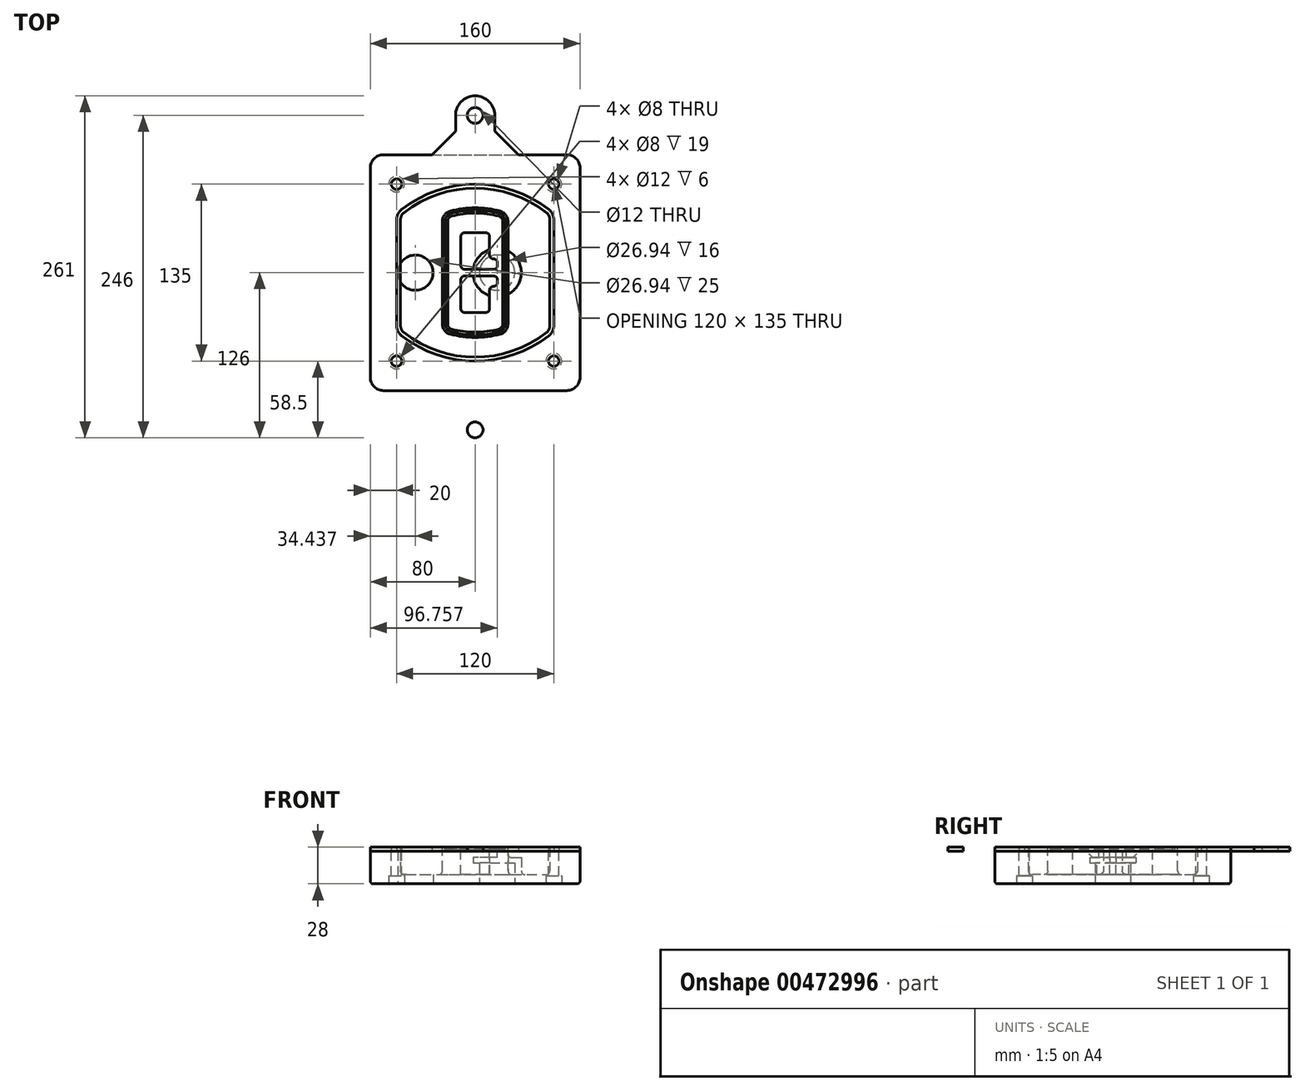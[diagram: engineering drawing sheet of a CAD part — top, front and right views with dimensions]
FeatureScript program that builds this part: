
annotation { "Feature Type Name" : "Feature", "Feature Type Description" : "" }
export const myFeature = defineFeature(function(context is Context, id is Id, definition is map)
    precondition{}
    {
        {
            var Q0;
            Q0=qCreatedBy(makeId("Top.planeOp"),FACE);
            var sketch = newSketch(context, id + "F0", { "sketchPlane" : qUnion([Q0])});
            skPoint(sketch, "E0.rect.middle", {"position": v(0, 0) * mm});
            skLineSegment(sketch, "E1.bottom", {"start": v(-70, -90) * mm, "end": v(70, -90) * mm});
            skLineSegment(sketch, "E1.top", {"start": v(-70, 90) * mm, "end": v(70, 90) * mm});
            skLineSegment(sketch, "E1.left", {"start": v(-80, -80) * mm, "end": v(-80, 80) * mm});
            skLineSegment(sketch, "E1.right", {"start": v(80, -80) * mm, "end": v(80, 80) * mm});
            skLineSegment(sketch, "E2", {"start": v(-80, 90) * mm, "end": v(80, -90) * mm, "construction": true});
            skLineSegment(sketch, "E3", {"start": v(80, 90) * mm, "end": v(-80, -90) * mm, "construction": true});
            skCircle(sketch, "E4", {"center": v(-60, 67.5) * mm, "radius": 4 * mm});
            skCircle(sketch, "E5", {"center": v(60, 67.5) * mm, "radius": 4 * mm});
            skCircle(sketch, "E6", {"center": v(60, -67.5) * mm, "radius": 4 * mm});
            skCircle(sketch, "E7", {"center": v(-60, -67.5) * mm, "radius": 4 * mm});
            skLineSegment(sketch, "E8", {"start": v(-60, 67.5) * mm, "end": v(60, 67.5) * mm, "construction": true});
            skLineSegment(sketch, "E9", {"start": v(60, 67.5) * mm, "end": v(60, -67.5) * mm, "construction": true});
            skLineSegment(sketch, "E10", {"start": v(60, -67.5) * mm, "end": v(-60, -67.5) * mm, "construction": true});
            skLineSegment(sketch, "E11", {"start": v(-60, -67.5) * mm, "end": v(-60, 67.5) * mm, "construction": true});
            skLineSegment(sketch, "E12", {"start": v(-60, 40.3) * mm, "end": v(-60, -40.3) * mm});
            skLineSegment(sketch, "E13", {"start": v(60, 40.3) * mm, "end": v(60, -40.3) * mm});
            skArc(sketch, "E14", {"start": v(56.15, 48.18) * mm, "mid": v(0, 67.5) * mm, "end": v(-56.15, 48.18) * mm});
            skArc(sketch, "E15", {"start": v(-56.15, -48.18) * mm, "mid": v(0, -67.5) * mm, "end": v(56.15, -48.18) * mm});
            skLineSegment(sketch, "E16", {"start": v(-60, 0) * mm, "end": v(60, 0) * mm, "construction": true});
            skPoint(sketch, "E17.visualSharp", {"position": v(-60, -45) * mm});
            skArc(sketch, "E17.filletArc", {"start": v(-60, -40.3) * mm, "mid": v(-58.99, -44.68) * mm, "end": v(-56.15, -48.18) * mm});
            skPoint(sketch, "E18.visualSharp", {"position": v(-60, 45) * mm});
            skArc(sketch, "E18.filletArc", {"start": v(-56.15, 48.18) * mm, "mid": v(-58.99, 44.68) * mm, "end": v(-60, 40.3) * mm});
            skPoint(sketch, "E19.visualSharp", {"position": v(60, 45) * mm});
            skArc(sketch, "E19.filletArc", {"start": v(60, 40.3) * mm, "mid": v(58.99, 44.68) * mm, "end": v(56.15, 48.18) * mm});
            skPoint(sketch, "E20.visualSharp", {"position": v(60, -45) * mm});
            skArc(sketch, "E20.filletArc", {"start": v(56.15, -48.18) * mm, "mid": v(58.99, -44.68) * mm, "end": v(60, -40.3) * mm});
            skPoint(sketch, "E21.visualSharp", {"position": v(-80, 90) * mm});
            skArc(sketch, "E21.filletArc", {"start": v(-70, 90) * mm, "mid": v(-77.07, 87.07) * mm, "end": v(-80, 80) * mm});
            skPoint(sketch, "E22.visualSharp", {"position": v(80, 90) * mm});
            skArc(sketch, "E22.filletArc", {"start": v(80, 80) * mm, "mid": v(77.07, 87.07) * mm, "end": v(70, 90) * mm});
            skPoint(sketch, "E23.visualSharp", {"position": v(80, -90) * mm});
            skArc(sketch, "E23.filletArc", {"start": v(70, -90) * mm, "mid": v(77.07, -87.07) * mm, "end": v(80, -80) * mm});
            skPoint(sketch, "E24.visualSharp", {"position": v(-80, -90) * mm});
            skArc(sketch, "E24.filletArc", {"start": v(-80, -80) * mm, "mid": v(-77.07, -87.07) * mm, "end": v(-70, -90) * mm});
            skArc(sketch, "E25.0", {"start": v(57, 40.3) * mm, "mid": v(56.3, 43.36) * mm, "end": v(54.3, 45.81) * mm});
            skLineSegment(sketch, "E25.1", {"start": v(57, 40.3) * mm, "end": v(57, -40.3) * mm});
            skArc(sketch, "E25.2", {"start": v(54.3, -45.81) * mm, "mid": v(56.3, -43.36) * mm, "end": v(57, -40.3) * mm});
            skArc(sketch, "E25.3", {"start": v(-54.3, -45.81) * mm, "mid": v(0, -64.5) * mm, "end": v(54.3, -45.81) * mm});
            skArc(sketch, "E25.4", {"start": v(-57, -40.3) * mm, "mid": v(-56.3, -43.36) * mm, "end": v(-54.3, -45.81) * mm});
            skArc(sketch, "E25.5", {"start": v(54.3, 45.81) * mm, "mid": v(0, 64.5) * mm, "end": v(-54.3, 45.81) * mm});
            skLineSegment(sketch, "E25.6", {"start": v(-57, 40.3) * mm, "end": v(-57, -40.3) * mm});
            skArc(sketch, "E25.7", {"start": v(-54.3, 45.81) * mm, "mid": v(-56.3, 43.36) * mm, "end": v(-57, 40.3) * mm});
            skArc(sketch, "E26.0", {"start": v(-58.62, 51.33) * mm, "mid": v(-62.58, 46.43) * mm, "end": v(-64, 40.3) * mm});
            skArc(sketch, "E26.1", {"start": v(58.62, 51.33) * mm, "mid": v(0, 71.5) * mm, "end": v(-58.62, 51.33) * mm});
            skArc(sketch, "E26.2", {"start": v(64, 40.3) * mm, "mid": v(62.58, 46.43) * mm, "end": v(58.62, 51.33) * mm});
            skLineSegment(sketch, "E26.3", {"start": v(64, 40.3) * mm, "end": v(64, -40.3) * mm});
            skArc(sketch, "E26.4", {"start": v(58.62, -51.33) * mm, "mid": v(62.58, -46.43) * mm, "end": v(64, -40.3) * mm});
            skLineSegment(sketch, "E26.5", {"start": v(-64, 40.3) * mm, "end": v(-64, -40.3) * mm});
            skArc(sketch, "E26.6", {"start": v(-58.62, -51.33) * mm, "mid": v(0, -71.5) * mm, "end": v(58.62, -51.33) * mm});
            skArc(sketch, "E26.7", {"start": v(-64, -40.3) * mm, "mid": v(-62.58, -46.43) * mm, "end": v(-58.62, -51.33) * mm});
            skSolve(sketch);
        }
        {
            var Q0;
            Q0=makeQuery(id+"F0.imprint","IMPRINT",FACE,{"disambiguationData":[TD([[makeQuery(id+"F0.imprint","IMPRINT",EDGE,{"derivedFrom":sQuery(id+"F0.wireOp",EDGE,"E1.bottom")}),1.0]])]});
            var Q1;
            Q1=makeQuery(id+"F0.imprint","IMPRINT",FACE,{"disambiguationData":[TD([[makeQuery(id+"F0.imprint","IMPRINT",EDGE,{"derivedFrom":sQuery(id+"F0.wireOp",EDGE,"E12")}),1.0]])]});
            var Q2;
            Q2=makeQuery(id+"F0.imprint","IMPRINT",FACE,{"disambiguationData":[TD([[makeQuery(id+"F0.imprint","IMPRINT",EDGE,{"derivedFrom":sQuery(id+"F0.wireOp",EDGE,"E25.0")}),1.0]])]});
            var Q3;
            Q3=makeQuery(id+"F0.imprint","IMPRINT",FACE,{"disambiguationData":[TD([[makeQuery(id+"F0.imprint","IMPRINT",EDGE,{"derivedFrom":sQuery(id+"F0.wireOp",EDGE,"E12")}),-1.0]])]});
            extrude(context, id + "F1", {"entities" : qUnion([Q0, Q1, Q2, Q3]), "oppositeDirection" : true, "depth" : 25 * mm});
        }
        {
            var Q0;
            Q0=makeQuery(id+"F0.imprint","IMPRINT",FACE,{"disambiguationData":[TD([[makeQuery(id+"F0.imprint","IMPRINT",EDGE,{"derivedFrom":sQuery(id+"F0.wireOp",EDGE,"E12")}),1.0]])]});
            extrude(context, id + "F2", {"entities" : qUnion([Q0]), "operationType" : NewBodyOperationType.ADD, "depth" : 3 * mm});
        }
        {
            var Q0;
            Q0=makeQuery(id+"F0.imprint","IMPRINT",FACE,{"disambiguationData":[TD([[makeQuery(id+"F0.imprint","IMPRINT",EDGE,{"derivedFrom":sQuery(id+"F0.wireOp",EDGE,"E25.0")}),1.0]])]});
            extrude(context, id + "F3", {"entities" : qUnion([Q0]), "operationType" : NewBodyOperationType.REMOVE, "oppositeDirection" : true, "depth" : 18 * mm});
        }
        {
            var Q0;
            Q0=makeQuery(id+"F2.opExtrude","CAP_FACE",FACE,{"disambiguationData":[OSD([sQuery(id+"F0.wireOp",EDGE,"E12"),sQuery(id+"F0.wireOp",EDGE,"E13"),sQuery(id+"F0.wireOp",EDGE,"E14"),sQuery(id+"F0.wireOp",EDGE,"E15"),sQuery(id+"F0.wireOp",EDGE,"E17.filletArc"),sQuery(id+"F0.wireOp",EDGE,"E18.filletArc"),sQuery(id+"F0.wireOp",EDGE,"E19.filletArc"),sQuery(id+"F0.wireOp",EDGE,"E20.filletArc"),sQuery(id+"F0.wireOp",EDGE,"E25.0"),sQuery(id+"F0.wireOp",EDGE,"E25.1"),sQuery(id+"F0.wireOp",EDGE,"E25.2"),sQuery(id+"F0.wireOp",EDGE,"E25.3"),sQuery(id+"F0.wireOp",EDGE,"E25.4"),sQuery(id+"F0.wireOp",EDGE,"E25.5"),sQuery(id+"F0.wireOp",EDGE,"E25.6"),sQuery(id+"F0.wireOp",EDGE,"E25.7")])],"isStart":false});
            var sketch = newSketch(context, id + "F4", { "sketchPlane" : qUnion([Q0])});
            skArc(sketch, "E27.0", {"start": v(-19.08, -46.97) * mm, "mid": v(0, -49.5) * mm, "end": v(19.08, -46.97) * mm});
            skArc(sketch, "E28.0", {"start": v(19.08, 46.97) * mm, "mid": v(0, 49.5) * mm, "end": v(-19.08, 46.97) * mm});
            skLineSegment(sketch, "E29", {"start": v(-25, 39.25) * mm, "end": v(-25, -39.25) * mm});
            skLineSegment(sketch, "E30", {"start": v(25, 39.25) * mm, "end": v(25, -39.25) * mm});
            skLineSegment(sketch, "E31", {"start": v(-25, 45.1) * mm, "end": v(25, 45.1) * mm, "construction": true});
            skLineSegment(sketch, "E32", {"start": v(-25, -45.1) * mm, "end": v(25, -45.1) * mm, "construction": true});
            skPoint(sketch, "E33.visualSharp", {"position": v(-25, 45.1) * mm});
            skArc(sketch, "E33.filletArc", {"start": v(-19.08, 46.97) * mm, "mid": v(-23.35, 44.11) * mm, "end": v(-25, 39.25) * mm});
            skPoint(sketch, "E34.visualSharp", {"position": v(25, 45.1) * mm});
            skArc(sketch, "E34.filletArc", {"start": v(25, 39.25) * mm, "mid": v(23.35, 44.11) * mm, "end": v(19.08, 46.97) * mm});
            skPoint(sketch, "E35.visualSharp", {"position": v(25, -45.1) * mm});
            skArc(sketch, "E35.filletArc", {"start": v(19.08, -46.97) * mm, "mid": v(23.35, -44.11) * mm, "end": v(25, -39.25) * mm});
            skPoint(sketch, "E36.visualSharp", {"position": v(-25, -45.1) * mm});
            skArc(sketch, "E36.filletArc", {"start": v(-25, -39.25) * mm, "mid": v(-23.35, -44.11) * mm, "end": v(-19.08, -46.97) * mm});
            skArc(sketch, "E37.0", {"start": v(54.3, 45.81) * mm, "mid": v(0, 64.5) * mm, "end": v(-54.3, 45.81) * mm});
            skArc(sketch, "E37.1", {"start": v(-54.3, 45.81) * mm, "mid": v(-56.3, 43.36) * mm, "end": v(-57, 40.3) * mm});
            skLineSegment(sketch, "E37.2", {"start": v(-57, 40.3) * mm, "end": v(-57, -40.3) * mm});
            skArc(sketch, "E37.3", {"start": v(-57, -40.3) * mm, "mid": v(-56.3, -43.36) * mm, "end": v(-54.3, -45.81) * mm});
            skArc(sketch, "E37.4", {"start": v(-54.3, -45.81) * mm, "mid": v(0, -64.5) * mm, "end": v(54.3, -45.81) * mm});
            skArc(sketch, "E37.5", {"start": v(54.3, -45.81) * mm, "mid": v(56.3, -43.36) * mm, "end": v(57, -40.3) * mm});
            skLineSegment(sketch, "E37.6", {"start": v(57, 40.3) * mm, "end": v(57, -40.3) * mm});
            skArc(sketch, "E37.7", {"start": v(57, 40.3) * mm, "mid": v(56.3, 43.36) * mm, "end": v(54.3, 45.81) * mm});
            skLineSegment(sketch, "E38.0", {"start": v(23, 39.25) * mm, "end": v(23, -39.25) * mm});
            skArc(sketch, "E38.1", {"start": v(18.56, -45.04) * mm, "mid": v(21.76, -42.9) * mm, "end": v(23, -39.25) * mm});
            skArc(sketch, "E38.2", {"start": v(-18.56, -45.04) * mm, "mid": v(0, -47.5) * mm, "end": v(18.56, -45.04) * mm});
            skArc(sketch, "E38.3", {"start": v(-23, -39.25) * mm, "mid": v(-21.76, -42.9) * mm, "end": v(-18.56, -45.04) * mm});
            skLineSegment(sketch, "E38.4", {"start": v(-23, 39.25) * mm, "end": v(-23, -39.25) * mm});
            skArc(sketch, "E38.5", {"start": v(23, 39.25) * mm, "mid": v(21.76, 42.9) * mm, "end": v(18.56, 45.04) * mm});
            skArc(sketch, "E38.6", {"start": v(-18.56, 45.04) * mm, "mid": v(-21.76, 42.9) * mm, "end": v(-23, 39.25) * mm});
            skArc(sketch, "E38.7", {"start": v(18.56, 45.04) * mm, "mid": v(0, 47.5) * mm, "end": v(-18.56, 45.04) * mm});
            skArc(sketch, "E39.0", {"start": v(21, 39.25) * mm, "mid": v(20.18, 41.68) * mm, "end": v(18.04, 43.1) * mm});
            skLineSegment(sketch, "E39.1", {"start": v(21, 39.25) * mm, "end": v(21, -39.25) * mm});
            skArc(sketch, "E39.2", {"start": v(18.04, -43.1) * mm, "mid": v(20.18, -41.68) * mm, "end": v(21, -39.25) * mm});
            skArc(sketch, "E39.3", {"start": v(-18.04, -43.1) * mm, "mid": v(0, -45.5) * mm, "end": v(18.04, -43.1) * mm});
            skArc(sketch, "E39.4", {"start": v(-21, -39.25) * mm, "mid": v(-20.18, -41.68) * mm, "end": v(-18.04, -43.1) * mm});
            skArc(sketch, "E39.5", {"start": v(18.04, 43.1) * mm, "mid": v(0, 45.5) * mm, "end": v(-18.04, 43.1) * mm});
            skLineSegment(sketch, "E39.6", {"start": v(-21, 39.25) * mm, "end": v(-21, -39.25) * mm});
            skArc(sketch, "E39.7", {"start": v(-18.04, 43.1) * mm, "mid": v(-20.18, 41.68) * mm, "end": v(-21, 39.25) * mm});
            skLineSegment(sketch, "E40", {"start": v(-25, 0) * mm, "end": v(25, 0) * mm, "construction": true});
            skLineSegment(sketch, "E41", {"start": v(-11, 5.5) * mm, "end": v(-11, 27.5) * mm});
            skLineSegment(sketch, "E42", {"start": v(-8, 30.5) * mm, "end": v(8, 30.5) * mm});
            skLineSegment(sketch, "E43", {"start": v(11, 27.5) * mm, "end": v(11, 13.5) * mm});
            skLineSegment(sketch, "E44", {"start": v(14, 10.5) * mm, "end": v(14, 10.5) * mm});
            skLineSegment(sketch, "E45", {"start": v(17, 7.5) * mm, "end": v(17, 5.5) * mm});
            skLineSegment(sketch, "E46", {"start": v(14, 2.5) * mm, "end": v(-8, 2.5) * mm});
            skPoint(sketch, "E47.visualSharp", {"position": v(-11, 30.5) * mm});
            skArc(sketch, "E47.filletArc", {"start": v(-8, 30.5) * mm, "mid": v(-10.12, 29.62) * mm, "end": v(-11, 27.5) * mm});
            skPoint(sketch, "E48.visualSharp", {"position": v(11, 30.5) * mm});
            skArc(sketch, "E48.filletArc", {"start": v(11, 27.5) * mm, "mid": v(10.12, 29.62) * mm, "end": v(8, 30.5) * mm});
            skPoint(sketch, "E49.visualSharp", {"position": v(11, 10.5) * mm});
            skArc(sketch, "E49.filletArc", {"start": v(11, 13.5) * mm, "mid": v(11.88, 11.38) * mm, "end": v(14, 10.5) * mm});
            skPoint(sketch, "E50.visualSharp", {"position": v(17, 10.5) * mm});
            skArc(sketch, "E50.filletArc", {"start": v(17, 7.5) * mm, "mid": v(16.12, 9.62) * mm, "end": v(14, 10.5) * mm});
            skPoint(sketch, "E51.visualSharp", {"position": v(17, 2.5) * mm});
            skArc(sketch, "E51.filletArc", {"start": v(14, 2.5) * mm, "mid": v(16.12, 3.38) * mm, "end": v(17, 5.5) * mm});
            skPoint(sketch, "E52.visualSharp", {"position": v(-11, 2.5) * mm});
            skArc(sketch, "E52.filletArc", {"start": v(-11, 5.5) * mm, "mid": v(-10.12, 3.38) * mm, "end": v(-8, 2.5) * mm});
            skLineSegment(sketch, "E53.0.MirrorCS", {"start": v(14, -2.5) * mm, "end": v(-8, -2.5) * mm});
            skArc(sketch, "E54.0.MirrorCS", {"start": v(-11, -5.5) * mm, "mid": v(-10.12, -3.38) * mm, "end": v(-8, -2.5) * mm});
            skLineSegment(sketch, "E55.0.MirrorCS", {"start": v(-11, -5.5) * mm, "end": v(-11, -27.5) * mm});
            skArc(sketch, "E56.0.MirrorCS", {"start": v(-8, -30.5) * mm, "mid": v(-10.12, -29.62) * mm, "end": v(-11, -27.5) * mm});
            skLineSegment(sketch, "E57.0.MirrorCS", {"start": v(-8, -30.5) * mm, "end": v(8, -30.5) * mm});
            skArc(sketch, "E58.0.MirrorCS", {"start": v(11, -27.5) * mm, "mid": v(10.12, -29.62) * mm, "end": v(8, -30.5) * mm});
            skLineSegment(sketch, "E59.0.MirrorCS", {"start": v(11, -27.5) * mm, "end": v(11, -13.5) * mm});
            skArc(sketch, "E60.0.MirrorCS", {"start": v(11, -13.5) * mm, "mid": v(11.88, -11.38) * mm, "end": v(14, -10.5) * mm});
            skArc(sketch, "E61.0.MirrorCS", {"start": v(17, -7.5) * mm, "mid": v(16.12, -9.62) * mm, "end": v(14, -10.5) * mm});
            skLineSegment(sketch, "E62.0.MirrorCS", {"start": v(17, -7.5) * mm, "end": v(17, -5.5) * mm});
            skArc(sketch, "E63.0.MirrorCS", {"start": v(14, -2.5) * mm, "mid": v(16.12, -3.38) * mm, "end": v(17, -5.5) * mm});
            skSolve(sketch);
        }
        {
            var Q0;
            Q0=makeQuery(id+"F4.imprint","IMPRINT",FACE,{"disambiguationData":[TD([[makeQuery(id+"F4.imprint","IMPRINT",EDGE,{"derivedFrom":sQuery(id+"F4.wireOp",EDGE,"E27.0")}),1.0]])]});
            var Q1;
            Q1=makeQuery(id+"F4.imprint","IMPRINT",FACE,{"disambiguationData":[TD([[makeQuery(id+"F4.imprint","IMPRINT",EDGE,{"derivedFrom":sQuery(id+"F4.wireOp",EDGE,"E38.0")}),-1.0]])]});
            var Q2;
            Q2=makeQuery(id+"F4.imprint","IMPRINT",FACE,{"disambiguationData":[TD([[makeQuery(id+"F4.imprint","IMPRINT",EDGE,{"derivedFrom":sQuery(id+"F4.wireOp",EDGE,"E39.0")}),1.0]])]});
            extrude(context, id + "F5", {"entities" : qUnion([Q0, Q1, Q2]), "operationType" : NewBodyOperationType.ADD, "endBound" : BoundingType.UP_TO_NEXT, "oppositeDirection" : true, "depth" : 25 * mm});
        }
        {
            var Q0;
            Q0=makeQuery(id+"F4.imprint","IMPRINT",FACE,{"disambiguationData":[TD([[makeQuery(id+"F4.imprint","IMPRINT",EDGE,{"derivedFrom":sQuery(id+"F4.wireOp",EDGE,"E38.0")}),-1.0]])]});
            extrude(context, id + "F6", {"entities" : qUnion([Q0]), "operationType" : NewBodyOperationType.REMOVE, "oppositeDirection" : true, "depth" : 2 * mm});
        }
        {
            var Q0;
            Q0=makeQuery(id+"F1.opExtrude","CAP_FACE",FACE,{"disambiguationData":[OSD([sQuery(id+"F0.wireOp",EDGE,"E1.bottom"),sQuery(id+"F0.wireOp",EDGE,"E1.top"),sQuery(id+"F0.wireOp",EDGE,"E1.left"),sQuery(id+"F0.wireOp",EDGE,"E1.right"),sQuery(id+"F0.wireOp",EDGE,"E4"),sQuery(id+"F0.wireOp",EDGE,"E5"),sQuery(id+"F0.wireOp",EDGE,"E6"),sQuery(id+"F0.wireOp",EDGE,"E7"),sQuery(id+"F0.wireOp",EDGE,"E21.filletArc"),sQuery(id+"F0.wireOp",EDGE,"E22.filletArc"),sQuery(id+"F0.wireOp",EDGE,"E23.filletArc"),sQuery(id+"F0.wireOp",EDGE,"E24.filletArc")])],"isStart":false});
            var sketch = newSketch(context, id + "F7", { "sketchPlane" : qUnion([Q0])});
            skCircle(sketch, "E64", {"center": v(16.76, 0) * mm, "radius": 13.47 * mm});
            skCircle(sketch, "E65", {"center": v(-45.56, 0) * mm, "radius": 13.47 * mm});
            skLineSegment(sketch, "E66", {"start": v(80, 0) * mm, "end": v(-80, 0) * mm});
            skCircle(sketch, "E67", {"center": v(16.76, 0) * mm, "radius": 18.47 * mm});
            skCircle(sketch, "E68", {"center": v(60, -67.5) * mm, "radius": 6 * mm});
            skCircle(sketch, "E69", {"center": v(-60, -67.5) * mm, "radius": 6 * mm});
            skCircle(sketch, "E70", {"center": v(-60, 67.5) * mm, "radius": 6 * mm});
            skCircle(sketch, "E71", {"center": v(60, 67.5) * mm, "radius": 6 * mm});
            skSolve(sketch);
        }
        {
            var Q0;
            {var subQ1=sQuery(id+"F7.wireOp",EDGE,"E66");var subQ4=sQuery(id+"F7.wireOp",EDGE,"E64");var subQ6=makeQuery(id+"F7.imprint","INTERSECT",VERTEX,{"disambiguationData":[OD(0.0)],"derivedFrom":[subQ4,subQ1]});Q0=makeQuery(id+"F7.imprint","IMPRINT",FACE,{"disambiguationData":[TD([[makeQuery(id+"F7.imprint","IMPRINT",EDGE,{"disambiguationData":[TD([[subQ6,-1.0]])],"derivedFrom":subQ4}),-1.0]])]});}
            var Q1;
            {var subQ0=sQuery(id+"F7.wireOp",EDGE,"E66");var subQ1=sQuery(id+"F7.wireOp",EDGE,"E64");var subQ3=makeQuery(id+"F7.imprint","INTERSECT",VERTEX,{"disambiguationData":[OD(0.0)],"derivedFrom":[subQ1,subQ0]});Q1=makeQuery(id+"F7.imprint","IMPRINT",FACE,{"disambiguationData":[TD([[makeQuery(id+"F7.imprint","IMPRINT",EDGE,{"disambiguationData":[TD([[subQ3,-1.0]])],"derivedFrom":subQ1}),1.0]])]});}
            var Q2;
            {var subQ0=sQuery(id+"F7.wireOp",EDGE,"E66");var subQ1=sQuery(id+"F7.wireOp",EDGE,"E64");var subQ3=makeQuery(id+"F7.imprint","INTERSECT",VERTEX,{"disambiguationData":[OD(0.0)],"derivedFrom":[subQ1,subQ0]});Q2=makeQuery(id+"F7.imprint","IMPRINT",FACE,{"disambiguationData":[TD([[makeQuery(id+"F7.imprint","IMPRINT",EDGE,{"disambiguationData":[TD([[subQ3,1.0]])],"derivedFrom":subQ1}),1.0]])]});}
            var Q3;
            {var subQ1=sQuery(id+"F7.wireOp",EDGE,"E66");var subQ4=sQuery(id+"F7.wireOp",EDGE,"E64");var subQ6=makeQuery(id+"F7.imprint","INTERSECT",VERTEX,{"disambiguationData":[OD(0.0)],"derivedFrom":[subQ4,subQ1]});Q3=makeQuery(id+"F7.imprint","IMPRINT",FACE,{"disambiguationData":[TD([[makeQuery(id+"F7.imprint","IMPRINT",EDGE,{"disambiguationData":[TD([[subQ6,1.0]])],"derivedFrom":subQ4}),-1.0]])]});}
            extrude(context, id + "F8", {"entities" : qUnion([Q0, Q1, Q2, Q3]), "operationType" : NewBodyOperationType.ADD, "oppositeDirection" : true, "depth" : 20 * mm});
        }
        {
            var Q0;
            {var subQ0=sQuery(id+"F7.wireOp",EDGE,"E66");var subQ1=sQuery(id+"F7.wireOp",EDGE,"E64");var subQ3=makeQuery(id+"F7.imprint","INTERSECT",VERTEX,{"disambiguationData":[OD(0.0)],"derivedFrom":[subQ1,subQ0]});Q0=makeQuery(id+"F7.imprint","IMPRINT",FACE,{"disambiguationData":[TD([[makeQuery(id+"F7.imprint","IMPRINT",EDGE,{"disambiguationData":[TD([[subQ3,-1.0]])],"derivedFrom":subQ1}),1.0]])]});}
            var Q1;
            {var subQ0=sQuery(id+"F7.wireOp",EDGE,"E66");var subQ1=sQuery(id+"F7.wireOp",EDGE,"E64");var subQ3=makeQuery(id+"F7.imprint","INTERSECT",VERTEX,{"disambiguationData":[OD(0.0)],"derivedFrom":[subQ1,subQ0]});Q1=makeQuery(id+"F7.imprint","IMPRINT",FACE,{"disambiguationData":[TD([[makeQuery(id+"F7.imprint","IMPRINT",EDGE,{"disambiguationData":[TD([[subQ3,1.0]])],"derivedFrom":subQ1}),1.0]])]});}
            extrude(context, id + "F9", {"entities" : qUnion([Q0, Q1]), "operationType" : NewBodyOperationType.REMOVE, "oppositeDirection" : true, "depth" : 16 * mm});
        }
        {
            var Q0;
            {var subQ0=sQuery(id+"F7.wireOp",EDGE,"E66");var subQ1=sQuery(id+"F7.wireOp",EDGE,"E65");var subQ3=makeQuery(id+"F7.imprint","INTERSECT",VERTEX,{"disambiguationData":[OD(0.0)],"derivedFrom":[subQ1,subQ0]});Q0=makeQuery(id+"F7.imprint","IMPRINT",FACE,{"disambiguationData":[TD([[makeQuery(id+"F7.imprint","IMPRINT",EDGE,{"disambiguationData":[TD([[subQ3,-1.0]])],"derivedFrom":subQ1}),1.0]])]});}
            var Q1;
            {var subQ0=sQuery(id+"F7.wireOp",EDGE,"E66");var subQ1=sQuery(id+"F7.wireOp",EDGE,"E65");var subQ3=makeQuery(id+"F7.imprint","INTERSECT",VERTEX,{"disambiguationData":[OD(0.0)],"derivedFrom":[subQ1,subQ0]});Q1=makeQuery(id+"F7.imprint","IMPRINT",FACE,{"disambiguationData":[TD([[makeQuery(id+"F7.imprint","IMPRINT",EDGE,{"disambiguationData":[TD([[subQ3,1.0]])],"derivedFrom":subQ1}),1.0]])]});}
            extrude(context, id + "F10", {"entities" : qUnion([Q0, Q1]), "operationType" : NewBodyOperationType.REMOVE, "oppositeDirection" : true, "depth" : 25 * mm});
        }
        {
            var Q0;
            Q0=makeQuery(id+"F7.imprint","IMPRINT",FACE,{"disambiguationData":[TD([[makeQuery(id+"F7.imprint","IMPRINT",EDGE,{"derivedFrom":sQuery(id+"F7.wireOp",EDGE,"E68")}),1.0]])]});
            var Q1;
            Q1=makeQuery(id+"F7.imprint","IMPRINT",FACE,{"disambiguationData":[TD([[makeQuery(id+"F7.imprint","IMPRINT",EDGE,{"derivedFrom":makeQuery(id+"F1.opExtrude","CAP_EDGE",EDGE,{"disambiguationData":[OSD([sQuery(id+"F0.wireOp",EDGE,"E5")])],"isStart":false})}),-1.0]])]});
            var Q2;
            Q2=makeQuery(id+"F7.imprint","IMPRINT",FACE,{"disambiguationData":[TD([[makeQuery(id+"F7.imprint","IMPRINT",EDGE,{"derivedFrom":sQuery(id+"F7.wireOp",EDGE,"E69")}),1.0]])]});
            var Q3;
            Q3=makeQuery(id+"F7.imprint","IMPRINT",FACE,{"disambiguationData":[TD([[makeQuery(id+"F7.imprint","IMPRINT",EDGE,{"derivedFrom":makeQuery(id+"F1.opExtrude","CAP_EDGE",EDGE,{"disambiguationData":[OSD([sQuery(id+"F0.wireOp",EDGE,"E4")])],"isStart":false})}),-1.0]])]});
            var Q4;
            Q4=makeQuery(id+"F7.imprint","IMPRINT",FACE,{"disambiguationData":[TD([[makeQuery(id+"F7.imprint","IMPRINT",EDGE,{"derivedFrom":sQuery(id+"F7.wireOp",EDGE,"E70")}),1.0]])]});
            var Q5;
            Q5=makeQuery(id+"F7.imprint","IMPRINT",FACE,{"disambiguationData":[TD([[makeQuery(id+"F7.imprint","IMPRINT",EDGE,{"derivedFrom":makeQuery(id+"F1.opExtrude","CAP_EDGE",EDGE,{"disambiguationData":[OSD([sQuery(id+"F0.wireOp",EDGE,"E7")])],"isStart":false})}),-1.0]])]});
            var Q6;
            Q6=makeQuery(id+"F7.imprint","IMPRINT",FACE,{"disambiguationData":[TD([[makeQuery(id+"F7.imprint","IMPRINT",EDGE,{"derivedFrom":sQuery(id+"F7.wireOp",EDGE,"E71")}),1.0]])]});
            var Q7;
            Q7=makeQuery(id+"F7.imprint","IMPRINT",FACE,{"disambiguationData":[TD([[makeQuery(id+"F7.imprint","IMPRINT",EDGE,{"derivedFrom":makeQuery(id+"F1.opExtrude","CAP_EDGE",EDGE,{"disambiguationData":[OSD([sQuery(id+"F0.wireOp",EDGE,"E6")])],"isStart":false})}),-1.0]])]});
            extrude(context, id + "F11", {"entities" : qUnion([Q0, Q1, Q2, Q3, Q4, Q5, Q6, Q7]), "operationType" : NewBodyOperationType.REMOVE, "oppositeDirection" : true, "depth" : 6 * mm});
        }
        {
            var Q0;
            Q0=makeQuery(id+"F9.boolean.opBoolean","COPY",FACE,{"derivedFrom":makeQuery(id+"F9.opExtrude","CAP_FACE",FACE,{"disambiguationData":[OSD([sQuery(id+"F7.wireOp",EDGE,"E64")])],"isStart":false})});
            var sketch = newSketch(context, id + "F12", { "sketchPlane" : qUnion([Q0])});
            skArc(sketch, "E72.0", {"start": v(11, 17.55) * mm, "mid": v(2.57, 11.82) * mm, "end": v(-1.54, 2.5) * mm});
            skArc(sketch, "E72.1", {"start": v(-1.54, -2.5) * mm, "mid": v(2.57, -11.82) * mm, "end": v(11, -17.55) * mm});
            skLineSegment(sketch, "E73", {"start": v(-1.54, -2.5) * mm, "end": v(14, -2.5) * mm});
            skLineSegment(sketch, "E74.0", {"start": v(14, 2.5) * mm, "end": v(-1.54, 2.5) * mm});
            skArc(sketch, "E74.1", {"start": v(14, 2.5) * mm, "mid": v(16.12, 3.38) * mm, "end": v(17, 5.5) * mm});
            skLineSegment(sketch, "E74.2", {"start": v(17, 7.5) * mm, "end": v(17, 5.5) * mm});
            skArc(sketch, "E74.3", {"start": v(17, 7.5) * mm, "mid": v(16.12, 9.62) * mm, "end": v(14, 10.5) * mm});
            skArc(sketch, "E74.4", {"start": v(11, 13.5) * mm, "mid": v(11.88, 11.38) * mm, "end": v(14, 10.5) * mm});
            skLineSegment(sketch, "E74.5", {"start": v(11, 17.55) * mm, "end": v(11, 13.5) * mm});
            skLineSegment(sketch, "E74.7", {"start": v(14, -2.5) * mm, "end": v(-1.54, -2.5) * mm});
            skArc(sketch, "E74.8", {"start": v(14, -2.5) * mm, "mid": v(16.12, -3.38) * mm, "end": v(17, -5.5) * mm});
            skLineSegment(sketch, "E74.9", {"start": v(17, -7.5) * mm, "end": v(17, -5.5) * mm});
            skArc(sketch, "E74.10", {"start": v(17, -7.5) * mm, "mid": v(16.12, -9.62) * mm, "end": v(14, -10.5) * mm});
            skArc(sketch, "E74.11", {"start": v(11, -13.5) * mm, "mid": v(11.88, -11.38) * mm, "end": v(14, -10.5) * mm});
            skLineSegment(sketch, "E74.12", {"start": v(11, -17.55) * mm, "end": v(11, -13.5) * mm});
            skPoint(sketch, "E75.orphan", {"position": v(11, -27.5) * mm});
            skPoint(sketch, "E76.orphan", {"position": v(-8, -2.5) * mm});
            skPoint(sketch, "E77.orphan", {"position": v(-8, 2.5) * mm});
            skPoint(sketch, "E78.orphan", {"position": v(11, 27.5) * mm});
            skSolve(sketch);
        }
        {
            var Q0;
            {var subQ7=sQuery(id+"F12.wireOp",EDGE,"E72.0");var subQ14=sQuery(id+"F12.wireOp",EDGE,"E72.1");var subQ16=sQuery(id+"F12.wireOp",EDGE,"E74.1");var subQ18=sQuery(id+"F12.wireOp",EDGE,"E74.8");Q0=qUnion([makeQuery(id+"F12.imprint","IMPRINT",FACE,{"disambiguationData":[TD([[makeQuery(id+"F12.imprint","IMPRINT",EDGE,{"derivedFrom":subQ7}),1.0]])]}),makeQuery(id+"F12.imprint","IMPRINT",FACE,{"disambiguationData":[TD([[makeQuery(id+"F12.imprint","IMPRINT",EDGE,{"derivedFrom":subQ14}),1.0]])]}),makeQuery(id+"F12.imprint","IMPRINT",FACE,{"disambiguationData":[TD([[makeQuery(id+"F12.imprint","IMPRINT",EDGE,{"derivedFrom":subQ16}),1.0]])]}),makeQuery(id+"F12.imprint","IMPRINT",FACE,{"disambiguationData":[TD([[makeQuery(id+"F12.imprint","IMPRINT",EDGE,{"derivedFrom":subQ18}),-1.0]])]})]);}
            var Q1;
            Q1=makeQuery(id+"F5.boolean.opBoolean","SPLIT",FACE,{"disambiguationData":[TD([makeQuery(id+"F5.opExtrude","SWEPT_FACE",FACE,{"disambiguationData":[OSD([sQuery(id+"F4.wireOp",EDGE,"E41")])]})])],"derivedFrom":makeQuery(id+"F3.boolean.opBoolean","COPY",FACE,{"derivedFrom":makeQuery(id+"F3.opExtrude","CAP_FACE",FACE,{"disambiguationData":[OSD([sQuery(id+"F0.wireOp",EDGE,"E25.0"),sQuery(id+"F0.wireOp",EDGE,"E25.1"),sQuery(id+"F0.wireOp",EDGE,"E25.2"),sQuery(id+"F0.wireOp",EDGE,"E25.3"),sQuery(id+"F0.wireOp",EDGE,"E25.4"),sQuery(id+"F0.wireOp",EDGE,"E25.5"),sQuery(id+"F0.wireOp",EDGE,"E25.6"),sQuery(id+"F0.wireOp",EDGE,"E25.7")])],"isStart":false})})});
            extrude(context, id + "F13", {"entities" : qUnion([Q0]), "operationType" : NewBodyOperationType.REMOVE, "endBound" : BoundingType.UP_TO_SURFACE, "endBoundEntityFace" : qUnion([Q1]), "depth" : 25 * mm});
        }
        {
            var Q0;
            Q0=makeQuery(id+"F3.boolean.opBoolean","COPY",EDGE,{"derivedFrom":makeQuery(id+"F3.opExtrude","CAP_EDGE",EDGE,{"disambiguationData":[OSD([sQuery(id+"F0.wireOp",EDGE,"E25.6")])],"isStart":false})});
            var Q1;
            Q1=makeQuery(id+"F8.boolean.opBoolean","INTERSECT",EDGE,{"derivedFrom":[makeQuery(id+"F5.opExtrude","SWEPT_FACE",FACE,{"disambiguationData":[OSD([sQuery(id+"F4.wireOp",EDGE,"E30")])]}),makeQuery(id+"F8.opExtrude","CAP_FACE",FACE,{"disambiguationData":[OSD([sQuery(id+"F7.wireOp",EDGE,"E67")])],"isStart":false})]});
            var Q2;
            Q2=makeQuery(id+"F8.boolean.opBoolean","INTERSECT",EDGE,{"disambiguationData":[OD(1.0)],"derivedFrom":[makeQuery(id+"F5.opExtrude","SWEPT_FACE",FACE,{"disambiguationData":[OSD([sQuery(id+"F4.wireOp",EDGE,"E30")])]}),makeQuery(id+"F8.opExtrude","SWEPT_FACE",FACE,{"disambiguationData":[OSD([sQuery(id+"F7.wireOp",EDGE,"E67")])]})]});
            var Q3;
            {var subQ0=sQuery(id+"F4.wireOp",EDGE,"E30");Q3=makeQuery(id+"F8.boolean.opBoolean","SPLIT",EDGE,{"disambiguationData":[TD([makeQuery(id+"F5.opExtrude","SWEPT_FACE",FACE,{"disambiguationData":[OSD([sQuery(id+"F4.wireOp",EDGE,"E35.filletArc")])]})])],"derivedFrom":makeQuery(id+"F5.opExtrude","CAP_EDGE",EDGE,{"disambiguationData":[OSD([subQ0])],"isStart":false})});}
            var Q4;
            {var subQ0=sQuery(id+"F0.wireOp",EDGE,"E25.7");var subQ1=sQuery(id+"F0.wireOp",EDGE,"E25.1");var subQ2=sQuery(id+"F0.wireOp",EDGE,"E25.6");var subQ3=sQuery(id+"F0.wireOp",EDGE,"E25.5");var subQ4=sQuery(id+"F0.wireOp",EDGE,"E25.4");var subQ5=sQuery(id+"F0.wireOp",EDGE,"E25.0");var subQ6=sQuery(id+"F0.wireOp",EDGE,"E25.2");var subQ7=sQuery(id+"F0.wireOp",EDGE,"E25.3");Q4=makeQuery(id+"F8.boolean.opBoolean","INTERSECT",EDGE,{"derivedFrom":[makeQuery(id+"F5.boolean.opBoolean","SPLIT",FACE,{"disambiguationData":[TD([makeQuery(id+"F2.opExtrude","SWEPT_FACE",FACE,{"disambiguationData":[OSD([subQ5])]})])],"derivedFrom":makeQuery(id+"F3.boolean.opBoolean","COPY",FACE,{"derivedFrom":makeQuery(id+"F3.opExtrude","CAP_FACE",FACE,{"disambiguationData":[OSD([subQ5,subQ1,subQ6,subQ7,subQ4,subQ3,subQ2,subQ0])],"isStart":false})})}),makeQuery(id+"F8.opExtrude","SWEPT_FACE",FACE,{"disambiguationData":[OSD([sQuery(id+"F7.wireOp",EDGE,"E67")])]})]});}
            var Q5;
            Q5=makeQuery(id+"F8.boolean.opBoolean","INTERSECT",EDGE,{"disambiguationData":[OD(0.0)],"derivedFrom":[makeQuery(id+"F5.opExtrude","SWEPT_FACE",FACE,{"disambiguationData":[OSD([sQuery(id+"F4.wireOp",EDGE,"E30")])]}),makeQuery(id+"F8.opExtrude","SWEPT_FACE",FACE,{"disambiguationData":[OSD([sQuery(id+"F7.wireOp",EDGE,"E67")])]})]});
            fillet(context, id + "F14", {"entities" : qUnion([Q0, Q1, Q2, Q3, Q4, Q5]), "radius" : 3 * mm, "tangentPropagation" : true, "allowEdgeOverflow" : false});
        }
        {
            var Q0;
            Q0=makeQuery(id+"F1.opExtrude","CAP_EDGE",EDGE,{"disambiguationData":[OSD([sQuery(id+"F0.wireOp",EDGE,"E1.bottom")])],"isStart":false});
            fillet(context, id + "F15", {"entities" : qUnion([Q0]), "radius" : 2 * mm, "tangentPropagation" : true, "allowEdgeOverflow" : false});
        }
        {
            var Q0;
            {var subQ0=sQuery(id+"F0.wireOp",EDGE,"E21.filletArc");var subQ1=sQuery(id+"F0.wireOp",EDGE,"E7");var subQ2=sQuery(id+"F0.wireOp",EDGE,"E6");var subQ3=sQuery(id+"F0.wireOp",EDGE,"E5");var subQ4=sQuery(id+"F0.wireOp",EDGE,"E4");var subQ5=sQuery(id+"F0.wireOp",EDGE,"E22.filletArc");var subQ6=sQuery(id+"F0.wireOp",EDGE,"E1.bottom");var subQ7=sQuery(id+"F0.wireOp",EDGE,"E1.right");var subQ8=sQuery(id+"F0.wireOp",EDGE,"E1.top");var subQ9=sQuery(id+"F0.wireOp",EDGE,"E1.left");var subQ10=sQuery(id+"F0.wireOp",EDGE,"E23.filletArc");var subQ11=sQuery(id+"F0.wireOp",EDGE,"E24.filletArc");Q0=makeQuery(id+"F2.boolean.opBoolean","SPLIT",FACE,{"disambiguationData":[TD([makeQuery(id+"F1.opExtrude","SWEPT_FACE",FACE,{"disambiguationData":[OSD([subQ6])]})])],"derivedFrom":makeQuery(id+"F1.opExtrude","CAP_FACE",FACE,{"disambiguationData":[OSD([subQ6,subQ8,subQ9,subQ7,subQ4,subQ3,subQ2,subQ1,subQ0,subQ5,subQ10,subQ11])],"isStart":true})});}
            var sketch = newSketch(context, id + "F16", { "sketchPlane" : qUnion([Q0])});
            skLineSegment(sketch, "E79.0", {"start": v(-70, 90) * mm, "end": v(70, 90) * mm});
            skArc(sketch, "E79.1", {"start": v(-70, 90) * mm, "mid": v(-77.07, 87.07) * mm, "end": v(-80, 80) * mm});
            skLineSegment(sketch, "E79.2", {"start": v(-80, -80) * mm, "end": v(-80, 80) * mm});
            skLineSegment(sketch, "E79.3", {"start": v(-70, -90) * mm, "end": v(70, -90) * mm});
            skArc(sketch, "E79.4", {"start": v(-80, -80) * mm, "mid": v(-77.07, -87.07) * mm, "end": v(-70, -90) * mm});
            skArc(sketch, "E79.5", {"start": v(70, -90) * mm, "mid": v(77.07, -87.07) * mm, "end": v(80, -80) * mm});
            skLineSegment(sketch, "E79.6", {"start": v(80, -80) * mm, "end": v(80, 80) * mm});
            skArc(sketch, "E79.7", {"start": v(80, 80) * mm, "mid": v(77.07, 87.07) * mm, "end": v(70, 90) * mm});
            skCircle(sketch, "E79.8", {"center": v(60, 67.5) * mm, "radius": 4 * mm});
            skCircle(sketch, "E79.9", {"center": v(-60, 67.5) * mm, "radius": 4 * mm});
            skCircle(sketch, "E79.10", {"center": v(-60, -67.5) * mm, "radius": 4 * mm});
            skCircle(sketch, "E79.11", {"center": v(60, -67.5) * mm, "radius": 4 * mm});
            skArc(sketch, "E79.12", {"start": v(56.15, 48.18) * mm, "mid": v(0, 67.5) * mm, "end": v(-56.15, 48.18) * mm});
            skArc(sketch, "E79.13", {"start": v(-56.15, 48.18) * mm, "mid": v(-58.99, 44.68) * mm, "end": v(-60, 40.3) * mm});
            skLineSegment(sketch, "E79.14", {"start": v(-60, 40.3) * mm, "end": v(-60, -40.3) * mm});
            skArc(sketch, "E79.15", {"start": v(-60, -40.3) * mm, "mid": v(-58.99, -44.68) * mm, "end": v(-56.15, -48.18) * mm});
            skArc(sketch, "E79.16", {"start": v(-56.15, -48.18) * mm, "mid": v(0, -67.5) * mm, "end": v(56.15, -48.18) * mm});
            skArc(sketch, "E79.17", {"start": v(56.15, -48.18) * mm, "mid": v(58.99, -44.68) * mm, "end": v(60, -40.3) * mm});
            skLineSegment(sketch, "E79.18", {"start": v(60, 40.3) * mm, "end": v(60, -40.3) * mm});
            skArc(sketch, "E79.19", {"start": v(60, 40.3) * mm, "mid": v(58.99, 44.68) * mm, "end": v(56.15, 48.18) * mm});
            skLineSegment(sketch, "E80", {"start": v(0, 90) * mm, "end": v(0, 120) * mm, "construction": true});
            skCircle(sketch, "E81", {"center": v(0, 120) * mm, "radius": 6 * mm});
            skLineSegment(sketch, "E82", {"start": v(-33, 90) * mm, "end": v(-15, 108) * mm});
            skLineSegment(sketch, "E83", {"start": v(-15, 108) * mm, "end": v(-15, 120) * mm});
            skLineSegment(sketch, "E84", {"start": v(33, 90) * mm, "end": v(15, 108) * mm});
            skLineSegment(sketch, "E85", {"start": v(15, 108) * mm, "end": v(15, 120) * mm});
            skArc(sketch, "E86", {"start": v(-15, 120) * mm, "mid": v(0, 135) * mm, "end": v(15, 120) * mm});
            skLineSegment(sketch, "E87", {"start": v(-76.98, 0) * mm, "end": v(80, 0) * mm, "construction": true});
            skArc(sketch, "E88.MirrorCS", {"start": v(-15, -120) * mm, "mid": v(0, -135) * mm, "end": v(15, -120) * mm});
            skCircle(sketch, "E89.MirrorC", {"center": v(0, -120) * mm, "radius": 6 * mm});
            skLineSegment(sketch, "E90.MirrorCS", {"start": v(15, -108) * mm, "end": v(15, -120) * mm});
            skLineSegment(sketch, "E91.MirrorCS", {"start": v(-15, -108) * mm, "end": v(-15, -120) * mm});
            skLineSegment(sketch, "E92.MirrorCS", {"start": v(0, -90) * mm, "end": v(0, -120) * mm, "construction": true});
            skLineSegment(sketch, "E93.MirrorCS", {"start": v(33, -90) * mm, "end": v(15, -108) * mm});
            skLineSegment(sketch, "E94.MirrorCS", {"start": v(-33, -90) * mm, "end": v(-15, -108) * mm});
            skSolve(sketch);
        }
        {
            var Q0;
            Q0=makeQuery(id+"F16.imprint","IMPRINT",FACE,{"disambiguationData":[TD([[makeQuery(id+"F16.imprint","IMPRINT",EDGE,{"derivedFrom":sQuery(id+"F16.wireOp",EDGE,"E81")}),-1.0]])]});
            var Q1;
            Q1=makeQuery(id+"F16.imprint","IMPRINT",FACE,{"disambiguationData":[TD([[makeQuery(id+"F16.imprint","IMPRINT",EDGE,{"derivedFrom":sQuery(id+"F16.wireOp",EDGE,"E89.MirrorC")}),1.0]])]});
            var Q2;
            {var subQ1=sQuery(id+"F16.wireOp",EDGE,"E79.1");Q2=makeQuery(id+"F16.imprint","IMPRINT",FACE,{"disambiguationData":[TD([[makeQuery(id+"F16.imprint","IMPRINT",EDGE,{"derivedFrom":subQ1}),1.0]])]});}
            var Q3;
            Q3=makeQuery(id+"F2.opExtrude","CAP_FACE",FACE,{"disambiguationData":[OSD([sQuery(id+"F0.wireOp",EDGE,"E12"),sQuery(id+"F0.wireOp",EDGE,"E13"),sQuery(id+"F0.wireOp",EDGE,"E14"),sQuery(id+"F0.wireOp",EDGE,"E15"),sQuery(id+"F0.wireOp",EDGE,"E17.filletArc"),sQuery(id+"F0.wireOp",EDGE,"E18.filletArc"),sQuery(id+"F0.wireOp",EDGE,"E19.filletArc"),sQuery(id+"F0.wireOp",EDGE,"E20.filletArc"),sQuery(id+"F0.wireOp",EDGE,"E25.0"),sQuery(id+"F0.wireOp",EDGE,"E25.1"),sQuery(id+"F0.wireOp",EDGE,"E25.2"),sQuery(id+"F0.wireOp",EDGE,"E25.3"),sQuery(id+"F0.wireOp",EDGE,"E25.4"),sQuery(id+"F0.wireOp",EDGE,"E25.5"),sQuery(id+"F0.wireOp",EDGE,"E25.6"),sQuery(id+"F0.wireOp",EDGE,"E25.7")])],"isStart":false});
            extrude(context, id + "F17", {"entities" : qUnion([Q0, Q1, Q2]), "endBound" : BoundingType.UP_TO_SURFACE, "endBoundEntityFace" : qUnion([Q3]), "depth" : 25 * mm});
        }
    });
